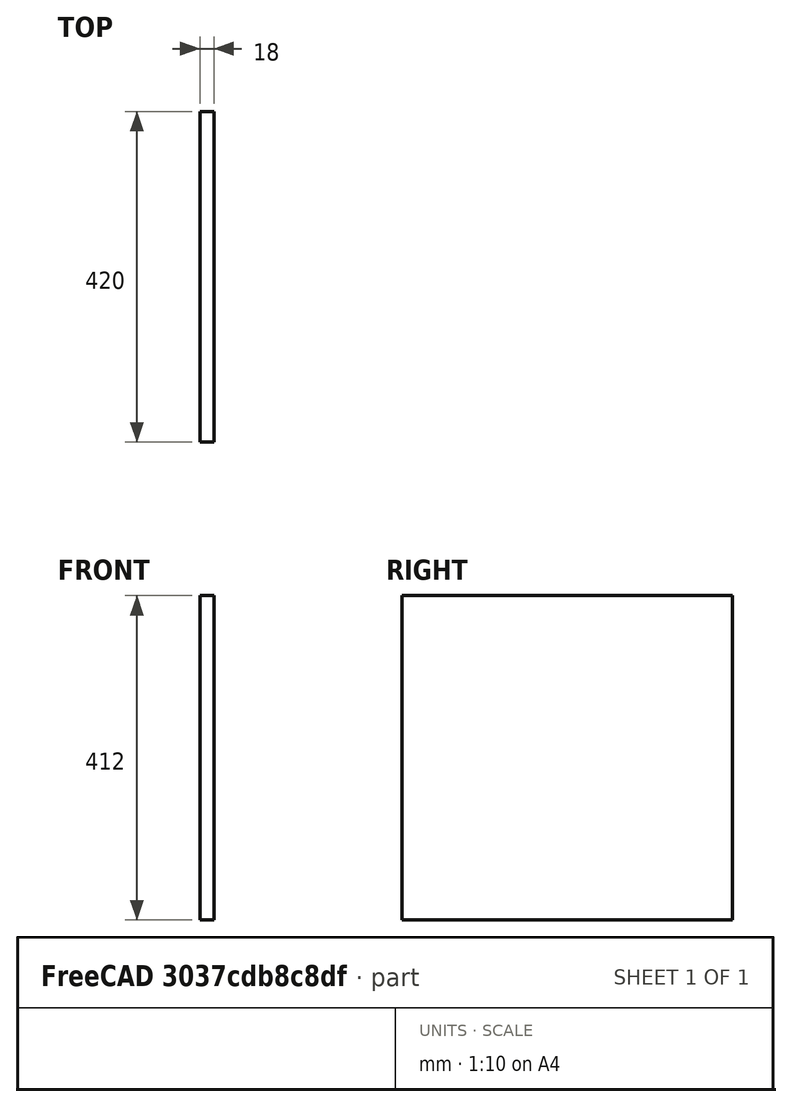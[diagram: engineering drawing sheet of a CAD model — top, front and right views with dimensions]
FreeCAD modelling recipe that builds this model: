
FCSTD DOCUMENT  (FreeCAD 0.18R4 (GitTag))
Label: front
License: All rights reserved
LicenseURL: http://en.wikipedia.org/wiki/All_rights_reserved
objects: Sketcher::SketchObject×1, PartDesign::Pad×1, PartDesign::Body×1
note: 4 computed .brp shape members not serialized (recipe doc carries the construction recipe); baked Part::Feature solids carry a one-line shape summary decoded from their .brp

FEATURE [Sketcher::SketchObject] Sketch
  MapMode = 5
  Placement = pos=(0,0,0) rot=(0.57735,0.57735,0.57735;2.0944rad)
  Support = -> [YZ_Plane]
  sketch-geometry (4):
    g0: LineSegment StartX=0 StartY=0 StartZ=0 EndX=-420 EndY=0 EndZ=0
    g1: LineSegment StartX=-420 StartY=0 StartZ=0 EndX=-420 EndY=412 EndZ=0
    g2: LineSegment StartX=-420 StartY=412 StartZ=0 EndX=0 EndY=412 EndZ=0
    g3: LineSegment StartX=0 StartY=412 StartZ=0 EndX=0 EndY=0 EndZ=0
  constraints (11):
    c: Coincident(g0,g1)
    c: Coincident(g1,g2)
    c: Coincident(g2,g3)
    c: Coincident(g3,g0)
    c: Horizontal(g0)
    c: Horizontal(g2)
    c: Vertical(g1)
    c: Vertical(g3)
    c: Coincident(g0,g-1)
    c: DistanceX(g0,g0) = 420
    c: DistanceY(g3,g3) = 412
FEATURE [PartDesign::Pad] Pad
  Length = 18
  Length2 = 100
  Placement = pos=(0,0,0) rot=(0.57735,0.57735,0.57735;2.0944rad)
  Profile = -> Sketch
  Type = 0
FEATURE [PartDesign::Body] Body
  Group = -> [Sketch,Pad]
  Origin = -> Origin
  Tip = -> Pad
